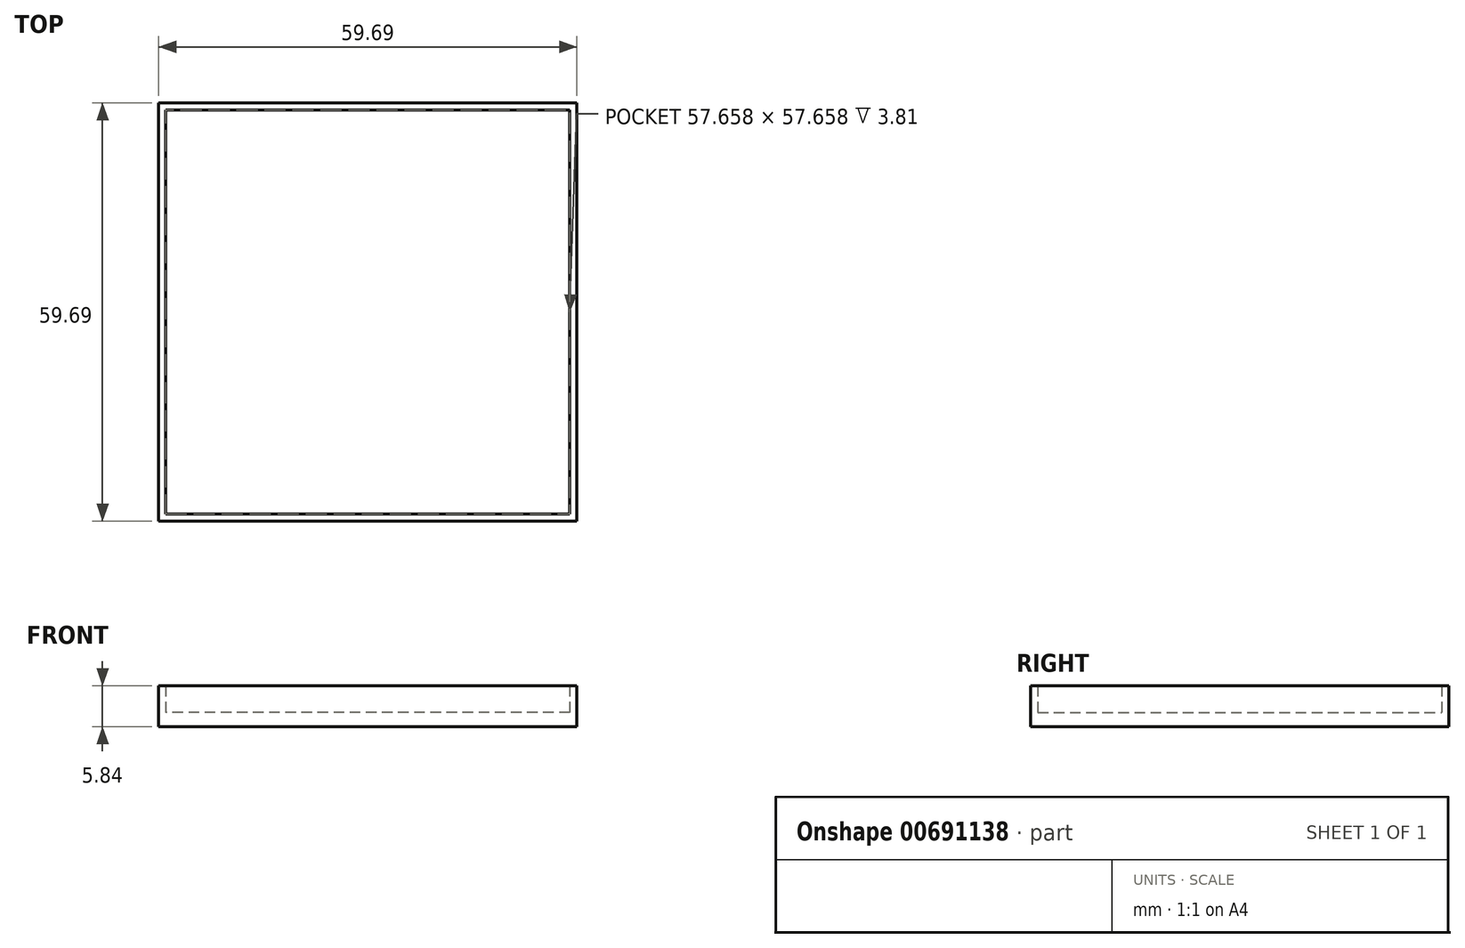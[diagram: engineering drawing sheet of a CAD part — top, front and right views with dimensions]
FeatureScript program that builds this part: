
annotation { "Feature Type Name" : "Feature", "Feature Type Description" : "" }
export const myFeature = defineFeature(function(context is Context, id is Id, definition is map)
    precondition{}
    {
        {
            var Q0;
            Q0=qCreatedBy(makeId("Top.planeOp"),FACE);
            var sketch = newSketch(context, id + "F0", { "sketchPlane" : qUnion([Q0])});
            skLineSegment(sketch, "E0.bottom", {"start": v(0, 0) * mm, "end": v(59.69, 0) * mm});
            skLineSegment(sketch, "E0.top", {"start": v(0, 59.7) * mm, "end": v(59.69, 59.7) * mm});
            skLineSegment(sketch, "E0.left", {"start": v(0, 0) * mm, "end": v(0, 59.69) * mm});
            skLineSegment(sketch, "E0.right", {"start": v(59.7, 0) * mm, "end": v(59.69, 59.7) * mm});
            skSolve(sketch);
        }
        {
            var Q0;
            Q0=qSketchRegion(id+"F0",true);
            extrude(context, id + "F1", {"entities" : qUnion([Q0]), "depth" : 2.03 * mm, "offsetDistance" : 25.4 * mm});
        }
        {
            var Q0;
            Q0=makeQuery(id+"F1.opExtrude","CAP_FACE",FACE,{"disambiguationData":[OSD([sQuery(id+"F0.wireOp",EDGE,"E0.bottom"),sQuery(id+"F0.wireOp",EDGE,"E0.top"),sQuery(id+"F0.wireOp",EDGE,"E0.left"),sQuery(id+"F0.wireOp",EDGE,"E0.right")])],"isStart":false});
            var sketch = newSketch(context, id + "F2", { "sketchPlane" : qUnion([Q0])});
            skLineSegment(sketch, "E1.0", {"start": v(58.67, 58.67) * mm, "end": v(1.02, 58.67) * mm});
            skLineSegment(sketch, "E1.1", {"start": v(58.67, 1.02) * mm, "end": v(58.67, 58.67) * mm});
            skLineSegment(sketch, "E1.2", {"start": v(1.02, 1.02) * mm, "end": v(58.67, 1.02) * mm});
            skLineSegment(sketch, "E1.3", {"start": v(1.02, 58.67) * mm, "end": v(1.02, 1.02) * mm});
            skSolve(sketch);
        }
        {
            var Q0;
            Q0=makeQuery(id+"F2.imprint","IMPRINT",FACE,{"disambiguationData":[TD([[makeQuery(id+"F2.imprint","IMPRINT",EDGE,{"derivedFrom":sQuery(id+"F2.wireOp",EDGE,"E1.0")}),-1.0]])]});
            extrude(context, id + "F3", {"entities" : qUnion([Q0]), "operationType" : NewBodyOperationType.ADD, "depth" : 3.8 * mm, "offsetDistance" : 25.4 * mm});
        }
    });
